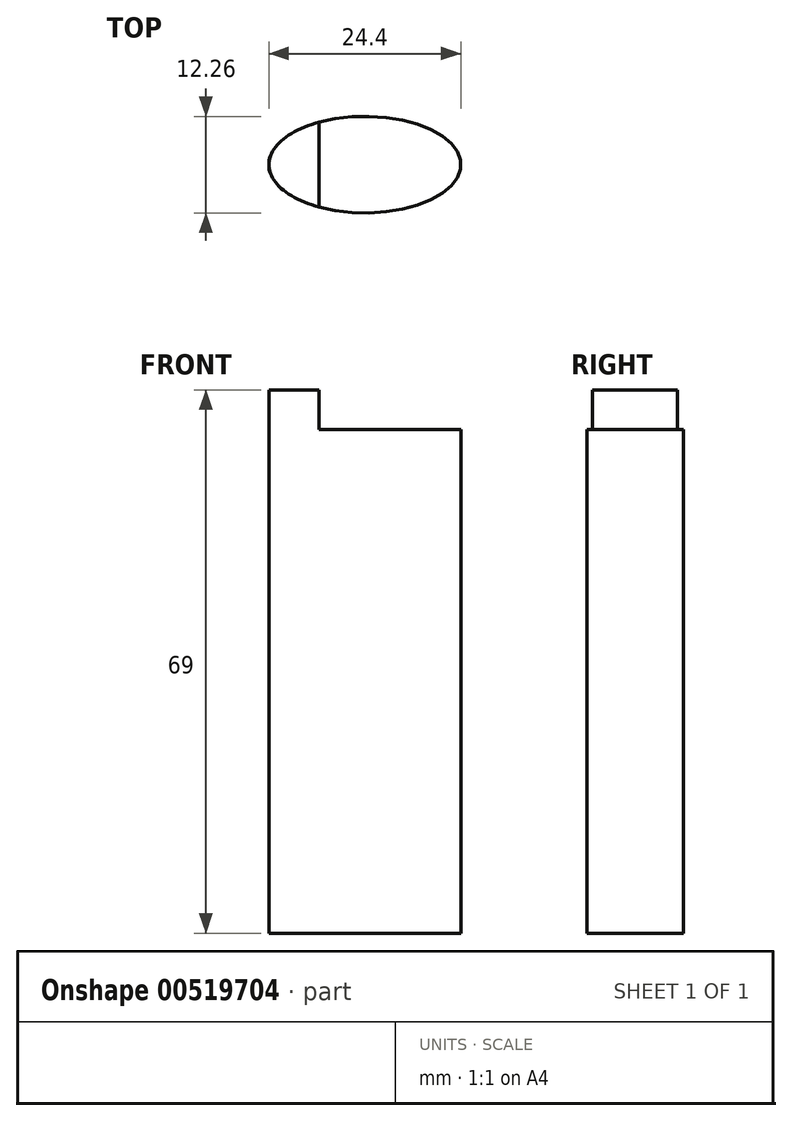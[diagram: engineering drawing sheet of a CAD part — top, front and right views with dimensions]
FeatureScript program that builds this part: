
annotation { "Feature Type Name" : "Feature", "Feature Type Description" : "" }
export const myFeature = defineFeature(function(context is Context, id is Id, definition is map)
    precondition{}
    {
        {
            var Q0;
            Q0=qCreatedBy(makeId("Top.planeOp"),FACE);
            var sketch = newSketch(context, id + "F0", { "sketchPlane" : qUnion([Q0])});
            skLineSegment(sketch, "E0", {"start": v(0, 0) * mm, "end": v(0, 6.13) * mm, "construction": true});
            skLineSegment(sketch, "E1", {"start": v(0, 0) * mm, "end": v(12.2, 0) * mm, "construction": true});
            skLineSegment(sketch, "E2", {"start": v(0, 0) * mm, "end": v(0, -6.13) * mm, "construction": true});
            skLineSegment(sketch, "E3", {"start": v(0, 0) * mm, "end": v(-12.2, 0) * mm, "construction": true});
            skEllipse(sketch, "E4", {"center": v(0, 0) * mm, "majorRadius": 6.13 * mm, "minorRadius": 12.2 * mm, "majorAxis": v(0, 1)});
            skSolve(sketch);
        }
        {
            var Q0;
            Q0 = qSketchRegion(id + "F0", true);
            extrude(context, id + "F1", {"entities" : qUnion([Q0]), "depth" : 64 * mm, "offsetDistance" : 25 * mm});
        }
        {
            var Q0;
            Q0=makeQuery(id+"F1.opExtrude","CAP_FACE",FACE,{"disambiguationData":[OSD([sQuery(id+"F0.wireOp",EDGE,"E4")])],"isStart":false});
            var sketch = newSketch(context, id + "F2", { "sketchPlane" : qUnion([Q0])});
            skLineSegment(sketch, "E5", {"start": v(12.2, 0) * mm, "end": v(-5.8, 0) * mm, "construction": true});
            skLineSegment(sketch, "E6", {"start": v(-5.8, -5.4) * mm, "end": v(-5.8, 5.4) * mm});
            skEllipticalArc(sketch, "E7.0", {});
            const initialGuessF2  = {"E7.0": [0, 0, -1, 0, 0.0122, 0.00613, 5.2078188009931745, 1.0753665061864126]};
            skSetInitialGuess(sketch, initialGuessF2);
            skSolve(sketch);
        }
        {
            var Q0;
            Q0 = qSketchRegion(id + "F2", true);
            extrude(context, id + "F3", {"entities" : qUnion([Q0]), "operationType" : NewBodyOperationType.ADD, "depth" : 5 * mm, "offsetDistance" : 25 * mm});
        }
    });
